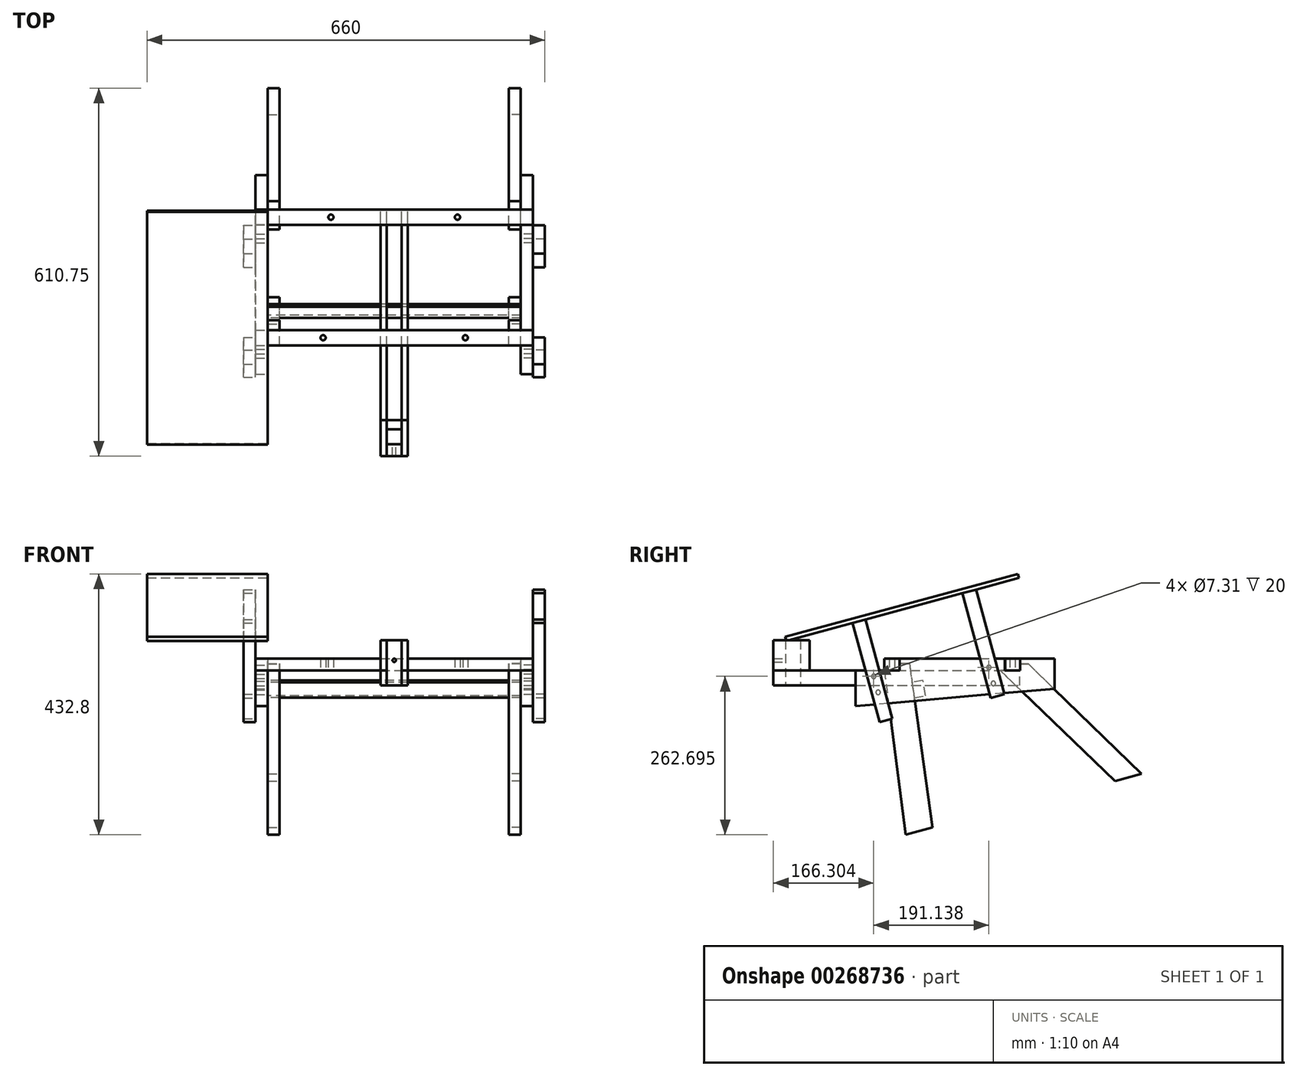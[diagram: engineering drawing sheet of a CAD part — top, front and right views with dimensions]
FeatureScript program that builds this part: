
annotation { "Feature Type Name" : "Feature", "Feature Type Description" : "" }
export const myFeature = defineFeature(function(context is Context, id is Id, definition is map)
    precondition{}
    {
        {
            var Q0;
            Q0=qCreatedBy(makeId("Top.planeOp"),FACE);
            var sketch = newSketch(context, id + "F0", { "sketchPlane" : qUnion([Q0])});
            skLineSegment(sketch, "E0.bottom", {"start": v(-230, -108) * mm, "end": v(230, -108) * mm});
            skLineSegment(sketch, "E0.top", {"start": v(-230, -133) * mm, "end": v(230, -133) * mm});
            skLineSegment(sketch, "E0.left", {"start": v(-230, -108) * mm, "end": v(-230, -133) * mm});
            skLineSegment(sketch, "E0.right", {"start": v(230, -108) * mm, "end": v(230, -133) * mm});
            skCircle(sketch, "E1", {"center": v(-118, -120.5) * mm, "radius": 4.3 * mm});
            skPoint(sketch, "E1.centerSnap0", {"position": v(-230, -120.5) * mm});
            skCircle(sketch, "E2.MirrorC", {"center": v(118, -120.5) * mm, "radius": 4.3 * mm});
            skLineSegment(sketch, "E3.bottom", {"start": v(-230, 92) * mm, "end": v(230, 92) * mm});
            skLineSegment(sketch, "E3.top", {"start": v(-230, 67) * mm, "end": v(230, 67) * mm});
            skLineSegment(sketch, "E3.left", {"start": v(-230, 92) * mm, "end": v(-230, 67) * mm});
            skLineSegment(sketch, "E3.right", {"start": v(230, 92) * mm, "end": v(230, 67) * mm});
            skCircle(sketch, "E4", {"center": v(-105, 79.5) * mm, "radius": 4.3 * mm});
            skPoint(sketch, "E4.centerSnap0", {"position": v(-230, 79.5) * mm});
            skCircle(sketch, "E5.MirrorC", {"center": v(105, 79.5) * mm, "radius": 4.3 * mm});
            skSolve(sketch);
        }
        {
            var Q0;
            Q0=makeQuery(id+"F0.imprint","IMPRINT",FACE,{"disambiguationData":[TD([[makeQuery(id+"F0.imprint","IMPRINT",EDGE,{"derivedFrom":sQuery(id+"F0.wireOp",EDGE,"E3.bottom")}),-1.0]])]});
            var Q1;
            Q1=makeQuery(id+"F0.imprint","IMPRINT",FACE,{"disambiguationData":[TD([[makeQuery(id+"F0.imprint","IMPRINT",EDGE,{"derivedFrom":sQuery(id+"F0.wireOp",EDGE,"E0.bottom")}),-1.0]])]});
            extrude(context, id + "F1", {"entities" : qUnion([Q0, Q1]), "depth" : 20 * mm});
        }
        {
            var Q0;
            Q0=qCreatedBy(makeId("Right.planeOp"),FACE);
            var sketch = newSketch(context, id + "F2", { "sketchPlane" : qUnion([Q0])});
            skLineSegment(sketch, "E6", {"start": v(-180.92, 0) * mm, "end": v(-107.8, 0) * mm});
            skLineSegment(sketch, "E7", {"start": v(-107.8, 19.75) * mm, "end": v(67.2, 19.75) * mm});
            skLineSegment(sketch, "E8", {"start": v(67.2, 19.75) * mm, "end": v(67.2, 0) * mm});
            skLineSegment(sketch, "E9", {"start": v(67.2, 0) * mm, "end": v(92.2, 0) * mm});
            skLineSegment(sketch, "E10", {"start": v(92.2, 0) * mm, "end": v(92.2, 19.6) * mm});
            skLineSegment(sketch, "E11", {"start": v(92.2, 19.6) * mm, "end": v(149.08, 19.6) * mm});
            skLineSegment(sketch, "E12", {"start": v(149.08, 19.6) * mm, "end": v(149.08, -30.27) * mm});
            skLineSegment(sketch, "E13", {"start": v(149.08, -30.27) * mm, "end": v(-180.92, -59.14) * mm});
            skLineSegment(sketch, "E14", {"start": v(-180.92, -59.14) * mm, "end": v(-180.92, 0) * mm});
            skLineSegment(sketch, "E15", {"start": v(-107.8, 19.75) * mm, "end": v(-107.8, 0) * mm});
            skCircle(sketch, "E16", {"center": v(-150.82, -9.81) * mm, "radius": 3.66 * mm});
            skCircle(sketch, "E17", {"center": v(-143.5, -36.3) * mm, "radius": 3.7 * mm});
            skCircle(sketch, "E18", {"center": v(40.32, 4.98) * mm, "radius": 3.66 * mm});
            skCircle(sketch, "E19", {"center": v(47.65, -21.5) * mm, "radius": 3.7 * mm});
            skSolve(sketch);
        }
        {
            var Q0;
            Q0=makeQuery(id+"F2.imprint","IMPRINT",FACE,{"disambiguationData":[TD([[makeQuery(id+"F2.imprint","IMPRINT",EDGE,{"derivedFrom":sQuery(id+"F2.wireOp",EDGE,"E6")}),-1.0]])]});
            var Q1;
            Q1=makeQuery(id+"F1.opExtrude","SWEPT_BODY",BODY,{"disambiguationData":[OSD([sQuery(id+"F0.wireOp",EDGE,"E0.bottom"),sQuery(id+"F0.wireOp",EDGE,"E0.top"),sQuery(id+"F0.wireOp",EDGE,"E0.left"),sQuery(id+"F0.wireOp",EDGE,"E0.right"),sQuery(id+"F0.wireOp",EDGE,"E1"),sQuery(id+"F0.wireOp",EDGE,"E2.MirrorC")])]});
            var Q2;
            Q2=makeQuery(id+"F1.opExtrude","CAP_VERTEX",VERTEX,{"disambiguationData":[OSD([sQuery(id+"F0.wireOp",EDGE,"E0.bottom"),sQuery(id+"F0.wireOp",EDGE,"E0.right")])],"isStart":true});
            extrude(context, id + "F3", {"entities" : qUnion([Q0]), "endBound" : BoundingType.UP_TO_VERTEX, "endBoundEntityBody" : qUnion([Q1]), "endBoundEntityVertex" : qUnion([Q2]), "depth" : 20 * mm, "hasSecondDirection" : true, "secondDirectionOppositeDirection" : false, "secondDirectionDepth" : 210 * mm});
        }
        {
            var Q0;
            Q0 = qSketchRegion(id + "F2", true);
            var Q1;
            Q1=makeQuery(id+"F1.opExtrude","CAP_VERTEX",VERTEX,{"disambiguationData":[OSD([sQuery(id+"F0.wireOp",EDGE,"E0.bottom"),sQuery(id+"F0.wireOp",EDGE,"E0.left")])],"isStart":false});
            extrude(context, id + "F4", {"entities" : qUnion([Q0]), "endBound" : BoundingType.UP_TO_VERTEX, "oppositeDirection" : true, "endBoundEntityVertex" : qUnion([Q1]), "depth" : 25.4 * mm, "hasSecondDirection" : true, "secondDirectionOppositeDirection" : true, "secondDirectionDepth" : 210 * mm});
        }
        {
            var Q0;
            Q0=qCreatedBy(makeId("Right.planeOp"),FACE);
            var sketch = newSketch(context, id + "F5", { "sketchPlane" : qUnion([Q0])});
            skLineSegment(sketch, "E20", {"start": v(-133.3, 0) * mm, "end": v(-97.62, -272.51) * mm});
            skLineSegment(sketch, "E21", {"start": v(-97.62, -272.51) * mm, "end": v(-53.4, -260.66) * mm});
            skLineSegment(sketch, "E22", {"start": v(-133.3, 0) * mm, "end": v(-108.69, 0) * mm});
            skLineSegment(sketch, "E23", {"start": v(-108.69, 0) * mm, "end": v(-108.69, 11.55) * mm});
            skLineSegment(sketch, "E24", {"start": v(-108.69, 11.55) * mm, "end": v(-91.27, 11.55) * mm});
            skLineSegment(sketch, "E25", {"start": v(-91.27, 11.55) * mm, "end": v(-53.4, -260.66) * mm});
            skLineSegment(sketch, "E26", {"start": v(59.32, 0) * mm, "end": v(92.16, 0) * mm});
            skLineSegment(sketch, "E27", {"start": v(92.16, 0) * mm, "end": v(92.16, 10.58) * mm});
            skLineSegment(sketch, "E28", {"start": v(92.16, 10.58) * mm, "end": v(106.16, 10.58) * mm});
            skLineSegment(sketch, "E29", {"start": v(106.16, 10.58) * mm, "end": v(293.63, -171.51) * mm});
            skLineSegment(sketch, "E30", {"start": v(293.63, -171.51) * mm, "end": v(249.63, -183.3) * mm});
            skLineSegment(sketch, "E31", {"start": v(249.63, -183.3) * mm, "end": v(59.32, 0) * mm});
            skLineSegment(sketch, "E32", {"start": v(92.16, 0) * mm, "end": v(59.32, 0) * mm});
            skSolve(sketch);
        }
        {
            var Q0;
            Q0=makeQuery(id+"F5.imprint","IMPRINT",FACE,{"disambiguationData":[TD([[makeQuery(id+"F5.imprint","IMPRINT",EDGE,{"derivedFrom":sQuery(id+"F5.wireOp",EDGE,"E27")}),-1.0]])]});
            var Q1;
            Q1=makeQuery(id+"F5.imprint","IMPRINT",FACE,{"disambiguationData":[TD([[makeQuery(id+"F5.imprint","IMPRINT",EDGE,{"derivedFrom":sQuery(id+"F5.wireOp",EDGE,"E20")}),1.0]])]});
            var Q2;
            Q2=makeQuery(id+"F4.opExtrude","CAP_FACE",FACE,{"disambiguationData":[OSD([sQuery(id+"F2.wireOp",EDGE,"E6"),sQuery(id+"F2.wireOp",EDGE,"E7"),sQuery(id+"F2.wireOp",EDGE,"E8"),sQuery(id+"F2.wireOp",EDGE,"E9"),sQuery(id+"F2.wireOp",EDGE,"E10"),sQuery(id+"F2.wireOp",EDGE,"E11"),sQuery(id+"F2.wireOp",EDGE,"E12"),sQuery(id+"F2.wireOp",EDGE,"E13"),sQuery(id+"F2.wireOp",EDGE,"E14"),sQuery(id+"F2.wireOp",EDGE,"E15"),sQuery(id+"F2.wireOp",EDGE,"E16"),sQuery(id+"F2.wireOp",EDGE,"E17"),sQuery(id+"F2.wireOp",EDGE,"E18"),sQuery(id+"F2.wireOp",EDGE,"E19")])],"isStart":true});
            var Q3;
            Q3=makeQuery(id+"F3.opExtrude","SWEPT_BODY",BODY,{"disambiguationData":[OSD([sQuery(id+"F2.wireOp",EDGE,"E6"),sQuery(id+"F2.wireOp",EDGE,"E7"),sQuery(id+"F2.wireOp",EDGE,"E8"),sQuery(id+"F2.wireOp",EDGE,"E9"),sQuery(id+"F2.wireOp",EDGE,"E10"),sQuery(id+"F2.wireOp",EDGE,"E11"),sQuery(id+"F2.wireOp",EDGE,"E12"),sQuery(id+"F2.wireOp",EDGE,"E13"),sQuery(id+"F2.wireOp",EDGE,"E14"),sQuery(id+"F2.wireOp",EDGE,"E15"),sQuery(id+"F2.wireOp",EDGE,"E16"),sQuery(id+"F2.wireOp",EDGE,"E17"),sQuery(id+"F2.wireOp",EDGE,"E18"),sQuery(id+"F2.wireOp",EDGE,"E19")])]});
            extrude(context, id + "F6", {"entities" : qUnion([Q0, Q1]), "endBound" : BoundingType.UP_TO_SURFACE, "oppositeDirection" : true, "endBoundEntityFace" : qUnion([Q2]), "endBoundEntityBody" : qUnion([Q3]), "depth" : 25 * mm, "hasSecondDirection" : true, "secondDirectionOppositeDirection" : true, "secondDirectionDepth" : 190 * mm});
        }
        {
            var Q0;
            Q0 = qSketchRegion(id + "F5", true);
            var Q1;
            Q1=makeQuery(id+"F3.opExtrude","CAP_FACE",FACE,{"disambiguationData":[OSD([sQuery(id+"F2.wireOp",EDGE,"E6"),sQuery(id+"F2.wireOp",EDGE,"E7"),sQuery(id+"F2.wireOp",EDGE,"E8"),sQuery(id+"F2.wireOp",EDGE,"E9"),sQuery(id+"F2.wireOp",EDGE,"E10"),sQuery(id+"F2.wireOp",EDGE,"E11"),sQuery(id+"F2.wireOp",EDGE,"E12"),sQuery(id+"F2.wireOp",EDGE,"E13"),sQuery(id+"F2.wireOp",EDGE,"E14"),sQuery(id+"F2.wireOp",EDGE,"E15"),sQuery(id+"F2.wireOp",EDGE,"E16"),sQuery(id+"F2.wireOp",EDGE,"E17"),sQuery(id+"F2.wireOp",EDGE,"E18"),sQuery(id+"F2.wireOp",EDGE,"E19")])],"isStart":true});
            extrude(context, id + "F7", {"entities" : qUnion([Q0]), "endBound" : BoundingType.UP_TO_SURFACE, "endBoundEntityFace" : qUnion([Q1]), "depth" : 25 * mm, "hasSecondDirection" : true, "secondDirectionOppositeDirection" : false, "secondDirectionDepth" : 190 * mm});
        }
        {
            var Q0;
            Q0=qCreatedBy(makeId("Top.planeOp"),FACE);
            var sketch = newSketch(context, id + "F8", { "sketchPlane" : qUnion([Q0])});
            skLineSegment(sketch, "E33.bottom", {"start": v(-22.5, -317.12) * mm, "end": v(-12.5, -317.12) * mm});
            skLineSegment(sketch, "E33.top", {"start": v(-22.5, 91.66) * mm, "end": v(-12.5, 91.66) * mm});
            skLineSegment(sketch, "E33.left", {"start": v(-22.5, -317.12) * mm, "end": v(-22.5, 91.66) * mm});
            skLineSegment(sketch, "E33.right", {"start": v(-12.5, -317.12) * mm, "end": v(-12.5, 91.66) * mm});
            skLineSegment(sketch, "E34.MirrorCS", {"start": v(22.5, -317.12) * mm, "end": v(12.5, -317.12) * mm});
            skLineSegment(sketch, "E35.MirrorCS", {"start": v(22.5, 91.66) * mm, "end": v(12.5, 91.66) * mm});
            skLineSegment(sketch, "E36.MirrorCS", {"start": v(22.5, -317.12) * mm, "end": v(22.5, 91.66) * mm});
            skLineSegment(sketch, "E37.MirrorCS", {"start": v(12.5, -317.12) * mm, "end": v(12.5, 91.66) * mm});
            skLineSegment(sketch, "E38.bottom", {"start": v(-12.5, -317.12) * mm, "end": v(12.5, -317.12) * mm});
            skLineSegment(sketch, "E38.top", {"start": v(-12.5, -297.12) * mm, "end": v(12.5, -297.12) * mm});
            skLineSegment(sketch, "E38.left", {"start": v(-12.5, -317.12) * mm, "end": v(-12.5, -297.12) * mm});
            skLineSegment(sketch, "E38.right", {"start": v(12.5, -317.12) * mm, "end": v(12.5, -297.12) * mm});
            skLineSegment(sketch, "E39.bottom", {"start": v(-12.5, -272.12) * mm, "end": v(12.5, -272.12) * mm});
            skLineSegment(sketch, "E39.top", {"start": v(-12.5, -257.12) * mm, "end": v(12.5, -257.12) * mm});
            skLineSegment(sketch, "E39.left", {"start": v(-12.5, -272.12) * mm, "end": v(-12.5, -257.12) * mm});
            skLineSegment(sketch, "E39.right", {"start": v(12.5, -272.12) * mm, "end": v(12.5, -257.12) * mm});
            skLineSegment(sketch, "E40", {"start": v(12.5, -257.12) * mm, "end": v(22.5, -257.12) * mm});
            skLineSegment(sketch, "E41", {"start": v(-12.5, -257.12) * mm, "end": v(-22.5, -257.12) * mm});
            skSolve(sketch);
        }
        {
            var Q0;
            Q0=makeQuery(id+"F8.imprint","IMPRINT",FACE,{"disambiguationData":[TD([[makeQuery(id+"F8.imprint","IMPRINT",EDGE,{"derivedFrom":sQuery(id+"F8.wireOp",EDGE,"E33.bottom")}),1.0]])]});
            var Q1;
            Q1=makeQuery(id+"F8.imprint","IMPRINT",FACE,{"disambiguationData":[TD([[makeQuery(id+"F8.imprint","IMPRINT",EDGE,{"derivedFrom":sQuery(id+"F8.wireOp",EDGE,"E34.MirrorCS")}),-1.0]])]});
            var Q2;
            {var subQ0=sQuery(id+"F8.wireOp",EDGE,"E35.MirrorCS");Q2=makeQuery(id+"F8.imprint","IMPRINT",FACE,{"disambiguationData":[TD([[makeQuery(id+"F8.imprint","IMPRINT",EDGE,{"derivedFrom":subQ0}),1.0]])]});}
            var Q3;
            {var subQ0=sQuery(id+"F8.wireOp",EDGE,"E33.top");Q3=makeQuery(id+"F8.imprint","IMPRINT",FACE,{"disambiguationData":[TD([[makeQuery(id+"F8.imprint","IMPRINT",EDGE,{"derivedFrom":subQ0}),-1.0]])]});}
            extrude(context, id + "F9", {"entities" : qUnion([Q0, Q1, Q2, Q3]), "oppositeDirection" : true, "depth" : 25 * mm});
        }
        {
            var Q0;
            Q0=makeQuery(id+"F8.imprint","IMPRINT",FACE,{"disambiguationData":[TD([[makeQuery(id+"F8.imprint","IMPRINT",EDGE,{"derivedFrom":sQuery(id+"F8.wireOp",EDGE,"E38.bottom")}),1.0]])]});
            var Q1;
            Q1=makeQuery(id+"F8.imprint","IMPRINT",FACE,{"disambiguationData":[TD([[makeQuery(id+"F8.imprint","IMPRINT",EDGE,{"derivedFrom":sQuery(id+"F8.wireOp",EDGE,"E39.bottom")}),1.0]])]});
            extrude(context, id + "F10", {"entities" : qUnion([Q0, Q1]), "depth" : 50 * mm, "hasSecondDirection" : true, "secondDirectionOppositeDirection" : true, "secondDirectionDepth" : 25 * mm});
        }
        {
            var Q0;
            {var subQ4=sQuery(id+"F8.wireOp",EDGE,"E33.bottom");Q0=makeQuery(id+"F8.imprint","IMPRINT",FACE,{"disambiguationData":[TD([[makeQuery(id+"F8.imprint","IMPRINT",EDGE,{"derivedFrom":subQ4}),1.0]])]});}
            var Q1;
            {var subQ4=sQuery(id+"F8.wireOp",EDGE,"E34.MirrorCS");Q1=makeQuery(id+"F8.imprint","IMPRINT",FACE,{"disambiguationData":[TD([[makeQuery(id+"F8.imprint","IMPRINT",EDGE,{"derivedFrom":subQ4}),-1.0]])]});}
            extrude(context, id + "F11", {"entities" : qUnion([Q0, Q1]), "depth" : 50 * mm});
        }
        {
            var Q0;
            Q0=qCreatedBy(makeId("Front.planeOp"),FACE);
            var sketch = newSketch(context, id + "F12", { "sketchPlane" : qUnion([Q0])});
            skCircle(sketch, "E42", {"center": v(0, 16.85) * mm, "radius": 3.96 * mm});
            skSolve(sketch);
        }
        {
            var Q0;
            Q0=sQuery(id+"F12.wireOp",VERTEX,"E42.center");
            var Q1;
            Q1=makeQuery(id+"F10.opExtrude","SWEPT_BODY",BODY,{"disambiguationData":[OSD([sQuery(id+"F8.wireOp",EDGE,"E38.bottom"),sQuery(id+"F8.wireOp",EDGE,"E38.top"),sQuery(id+"F8.wireOp",EDGE,"E38.left"),sQuery(id+"F8.wireOp",EDGE,"E38.right")])]});
            hole(context, id + "F13", {"style" : HoleStyle.SIMPLE, "endStyle" : HoleEndStyle.THROUGH, "oppositeDirection" : true, "standardTappedOrClearance" : lookupTablePath({ "standard" : "ISO", "fit" : "Normal", "size" : "M5", "type" : "Clearance" }), "standardBlindInLast" : lookupTablePath({ "fit" : "Standard", "standard" : "ISO", "size" : "M5", "type" : "Clearance" }), "holeDiameter" : 5.5 * mm, "tappedDepth" : 12 * mm, "tapClearance" : 3, "locations" : qUnion([Q0]), "scope" : qUnion([Q1])});
        }
        {
            var Q0;
            Q0=qCreatedBy(makeId("Right.planeOp"),FACE);
            var sketch = newSketch(context, id + "F14", { "sketchPlane" : qUnion([Q0])});
            skLineSegment(sketch, "E43", {"start": v(-87.65, -19.68) * mm, "end": v(-82.92, -45.38) * mm});
            skLineSegment(sketch, "E44", {"start": v(-82.92, -45.38) * mm, "end": v(-64.55, -42) * mm});
            skLineSegment(sketch, "E45", {"start": v(-64.55, -42) * mm, "end": v(-69.29, -16.3) * mm});
            skLineSegment(sketch, "E46", {"start": v(-69.29, -16.3) * mm, "end": v(-87.65, -19.68) * mm});
            skSolve(sketch);
        }
        {
            var Q0;
            Q0 = qSketchRegion(id + "F14", true);
            extrude(context, id + "F15", {"entities" : qUnion([Q0]), "endBound" : BoundingType.SYMMETRIC, "depth" : 420 * mm});
        }
        {
            var Q0;
            Q0=qCreatedBy(makeId("Right.planeOp"),FACE);
            var sketch = newSketch(context, id + "F16", { "sketchPlane" : qUnion([Q0])});
            skLineSegment(sketch, "E47", {"start": v(-141.11, -85.67) * mm, "end": v(-185.7, 78.7) * mm});
            skLineSegment(sketch, "E48", {"start": v(-185.7, 78.7) * mm, "end": v(-164.42, 84.48) * mm});
            skLineSegment(sketch, "E49", {"start": v(-164.42, 84.48) * mm, "end": v(-119.84, -79.9) * mm});
            skLineSegment(sketch, "E50", {"start": v(-119.84, -79.9) * mm, "end": v(-141.11, -85.67) * mm});
            skLineSegment(sketch, "E51", {"start": v(43.21, -45.72) * mm, "end": v(-3.9, 128) * mm});
            skLineSegment(sketch, "E52", {"start": v(-3.9, 128) * mm, "end": v(19.1, 134.24) * mm});
            skLineSegment(sketch, "E53", {"start": v(19.1, 134.24) * mm, "end": v(66.21, -39.48) * mm});
            skLineSegment(sketch, "E54", {"start": v(66.21, -39.48) * mm, "end": v(43.21, -45.72) * mm});
            skLineSegment(sketch, "E55", {"start": v(-3.9, 128) * mm, "end": v(-164.42, 84.48) * mm});
            skLineSegment(sketch, "E56", {"start": v(-185.7, 78.7) * mm, "end": v(-295.84, 48.84) * mm});
            skLineSegment(sketch, "E57", {"start": v(-295.84, 48.84) * mm, "end": v(-297.67, 55.6) * mm});
            skLineSegment(sketch, "E58", {"start": v(-297.67, 55.6) * mm, "end": v(88.38, 160.29) * mm});
            skLineSegment(sketch, "E59", {"start": v(88.38, 160.29) * mm, "end": v(90.21, 153.53) * mm});
            skLineSegment(sketch, "E60", {"start": v(90.21, 153.53) * mm, "end": v(19.1, 134.24) * mm});
            skSolve(sketch);
        }
        {
            var Q0;
            Q0=makeQuery(id+"F16.imprint","IMPRINT",FACE,{"disambiguationData":[TD([[makeQuery(id+"F16.imprint","IMPRINT",EDGE,{"derivedFrom":sQuery(id+"F16.wireOp",EDGE,"E51")}),-1.0]])]});
            var Q1;
            Q1=makeQuery(id+"F16.imprint","IMPRINT",FACE,{"disambiguationData":[TD([[makeQuery(id+"F16.imprint","IMPRINT",EDGE,{"derivedFrom":sQuery(id+"F16.wireOp",EDGE,"E47")}),-1.0]])]});
            var Q2;
            Q2=makeQuery(id+"F3.opExtrude","CAP_FACE",FACE,{"disambiguationData":[OSD([dummyQuery(id+"F3.vertexPlane.planeOp",FACE)])],"isStart":false});
            extrude(context, id + "F17", {"entities" : qUnion([Q0, Q1]), "operationType" : NewBodyOperationType.ADD, "endBoundEntityFace" : qUnion([Q2]), "depth" : 250 * mm, "hasSecondDirection" : true, "secondDirectionOppositeDirection" : false, "secondDirectionDepth" : 230 * mm});
        }
        {
            var Q0;
            Q0=makeQuery(id+"F16.imprint","IMPRINT",FACE,{"disambiguationData":[TD([[makeQuery(id+"F16.imprint","IMPRINT",EDGE,{"derivedFrom":sQuery(id+"F16.wireOp",EDGE,"E47")}),-1.0]])]});
            var Q1;
            Q1=makeQuery(id+"F16.imprint","IMPRINT",FACE,{"disambiguationData":[TD([[makeQuery(id+"F16.imprint","IMPRINT",EDGE,{"derivedFrom":sQuery(id+"F16.wireOp",EDGE,"E51")}),-1.0]])]});
            extrude(context, id + "F18", {"entities" : qUnion([Q0, Q1]), "operationType" : NewBodyOperationType.ADD, "oppositeDirection" : true, "depth" : 250 * mm, "hasSecondDirection" : true, "secondDirectionOppositeDirection" : true, "secondDirectionDepth" : 230 * mm});
        }
        {
            var Q0;
            Q0=makeQuery(id+"F16.imprint","IMPRINT",FACE,{"disambiguationData":[TD([[makeQuery(id+"F16.imprint","IMPRINT",EDGE,{"derivedFrom":sQuery(id+"F16.wireOp",EDGE,"E48")}),1.0]])]});
            extrude(context, id + "F19", {"entities" : qUnion([Q0]), "oppositeDirection" : true, "depth" : 410 * mm, "hasSecondDirection" : true, "secondDirectionOppositeDirection" : true, "secondDirectionDepth" : 210 * mm});
        }
    });
